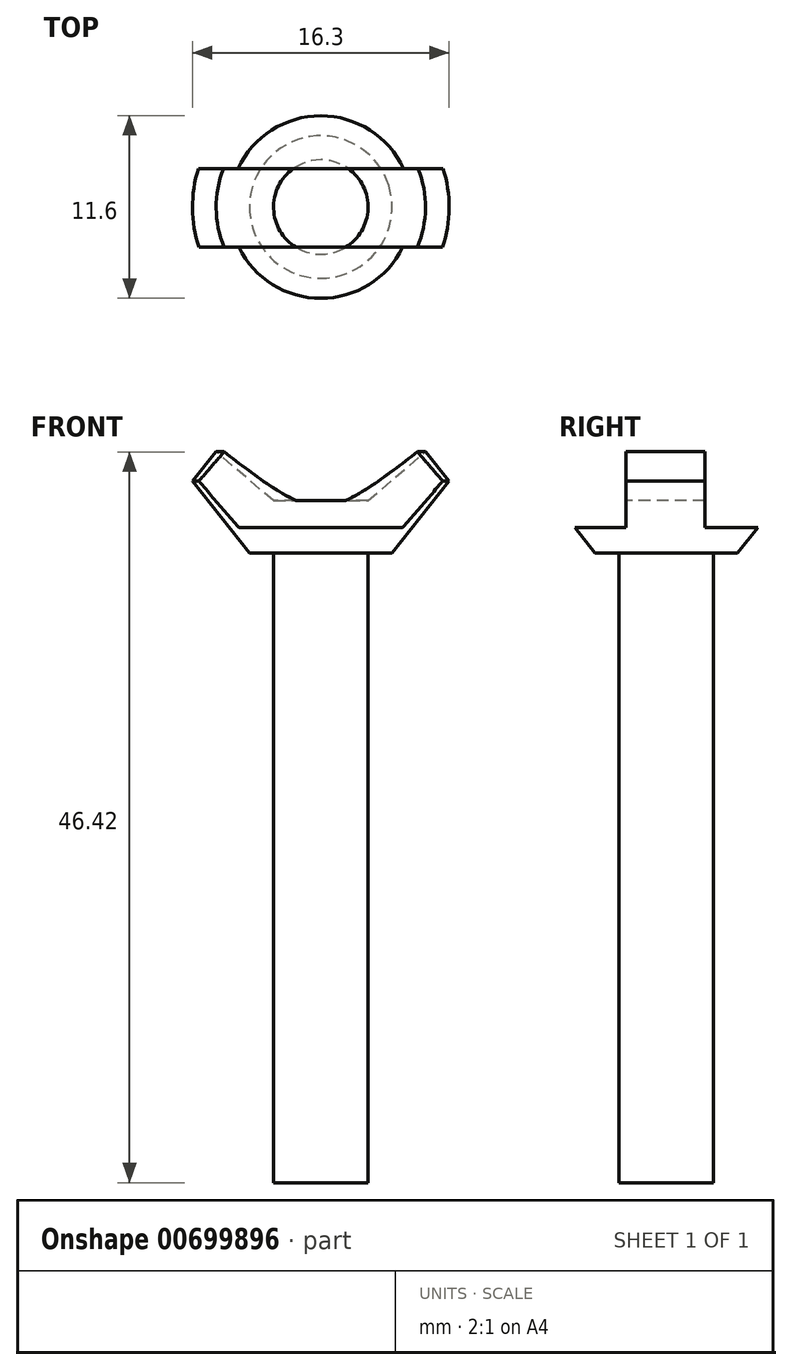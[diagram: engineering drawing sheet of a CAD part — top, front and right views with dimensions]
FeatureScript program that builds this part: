
annotation { "Feature Type Name" : "Feature", "Feature Type Description" : "" }
export const myFeature = defineFeature(function(context is Context, id is Id, definition is map)
    precondition{}
    {
        {
            var Q0;
            Q0=qCreatedBy(makeId("Front.planeOp"),FACE);
            var sketch = newSketch(context, id + "F0", { "sketchPlane" : qUnion([Q0])});
            skLineSegment(sketch, "E0", {"start": v(0, 0) * mm, "end": v(0, 43.33) * mm});
            skLineSegment(sketch, "E1", {"start": v(0, 43.33) * mm, "end": v(3, 43.33) * mm});
            skLineSegment(sketch, "E2", {"start": v(3, 43.33) * mm, "end": v(6.65, 46.42) * mm});
            skLineSegment(sketch, "E3", {"start": v(6.65, 46.42) * mm, "end": v(8.15, 44.56) * mm});
            skLineSegment(sketch, "E4", {"start": v(8.15, 44.56) * mm, "end": v(4.53, 40) * mm});
            skLineSegment(sketch, "E5", {"start": v(4.53, 40) * mm, "end": v(3, 40) * mm});
            skLineSegment(sketch, "E6", {"start": v(3, 40) * mm, "end": v(3, 0) * mm});
            skLineSegment(sketch, "E7", {"start": v(0, 0) * mm, "end": v(3, 0) * mm});
            skSolve(sketch);
        }
        {
            var Q0;
            Q0=makeQuery(id+"F0.imprint","IMPRINT",FACE,{"disambiguationData":[TD([[makeQuery(id+"F0.imprint","IMPRINT",EDGE,{"derivedFrom":sQuery(id+"F0.wireOp",EDGE,"E0")}),-1.0]])]});
            var Q1;
            Q1=sQuery(id+"F0.wireOp",EDGE,"E0");
            revolve(context, id + "F1", {"entities" : qUnion([Q0]), "axis" : qUnion([Q1]), "revolveType" : RevolveType.FULL});
        }
        {
            var Q0;
            Q0=qCreatedBy(makeId("Right.planeOp"),FACE);
            var sketch = newSketch(context, id + "F2", { "sketchPlane" : qUnion([Q0])});
            skLineSegment(sketch, "E8.bottom", {"start": v(-11.45, 53.34) * mm, "end": v(-2.56, 53.34) * mm});
            skLineSegment(sketch, "E8.top", {"start": v(-11.45, 41.6) * mm, "end": v(-2.56, 41.6) * mm});
            skLineSegment(sketch, "E8.left", {"start": v(-11.45, 53.34) * mm, "end": v(-11.45, 41.6) * mm});
            skLineSegment(sketch, "E8.right", {"start": v(-2.56, 53.34) * mm, "end": v(-2.56, 41.6) * mm});
            skLineSegment(sketch, "E9.bottom", {"start": v(10.06, 53.34) * mm, "end": v(2.44, 53.34) * mm});
            skLineSegment(sketch, "E9.top", {"start": v(10.06, 41.6) * mm, "end": v(2.44, 41.6) * mm});
            skLineSegment(sketch, "E9.left", {"start": v(10.06, 53.34) * mm, "end": v(10.06, 41.6) * mm});
            skLineSegment(sketch, "E9.right", {"start": v(2.44, 53.34) * mm, "end": v(2.44, 41.6) * mm});
            skSolve(sketch);
        }
        {
            var Q0;
            Q0 = qSketchRegion(id + "F2", true);
            extrude(context, id + "F3", {"entities" : qUnion([Q0]), "operationType" : NewBodyOperationType.REMOVE, "endBound" : BoundingType.SYMMETRIC, "oppositeDirection" : true, "depth" : 40 * mm, "offsetDistance" : 25 * mm});
        }
    });
